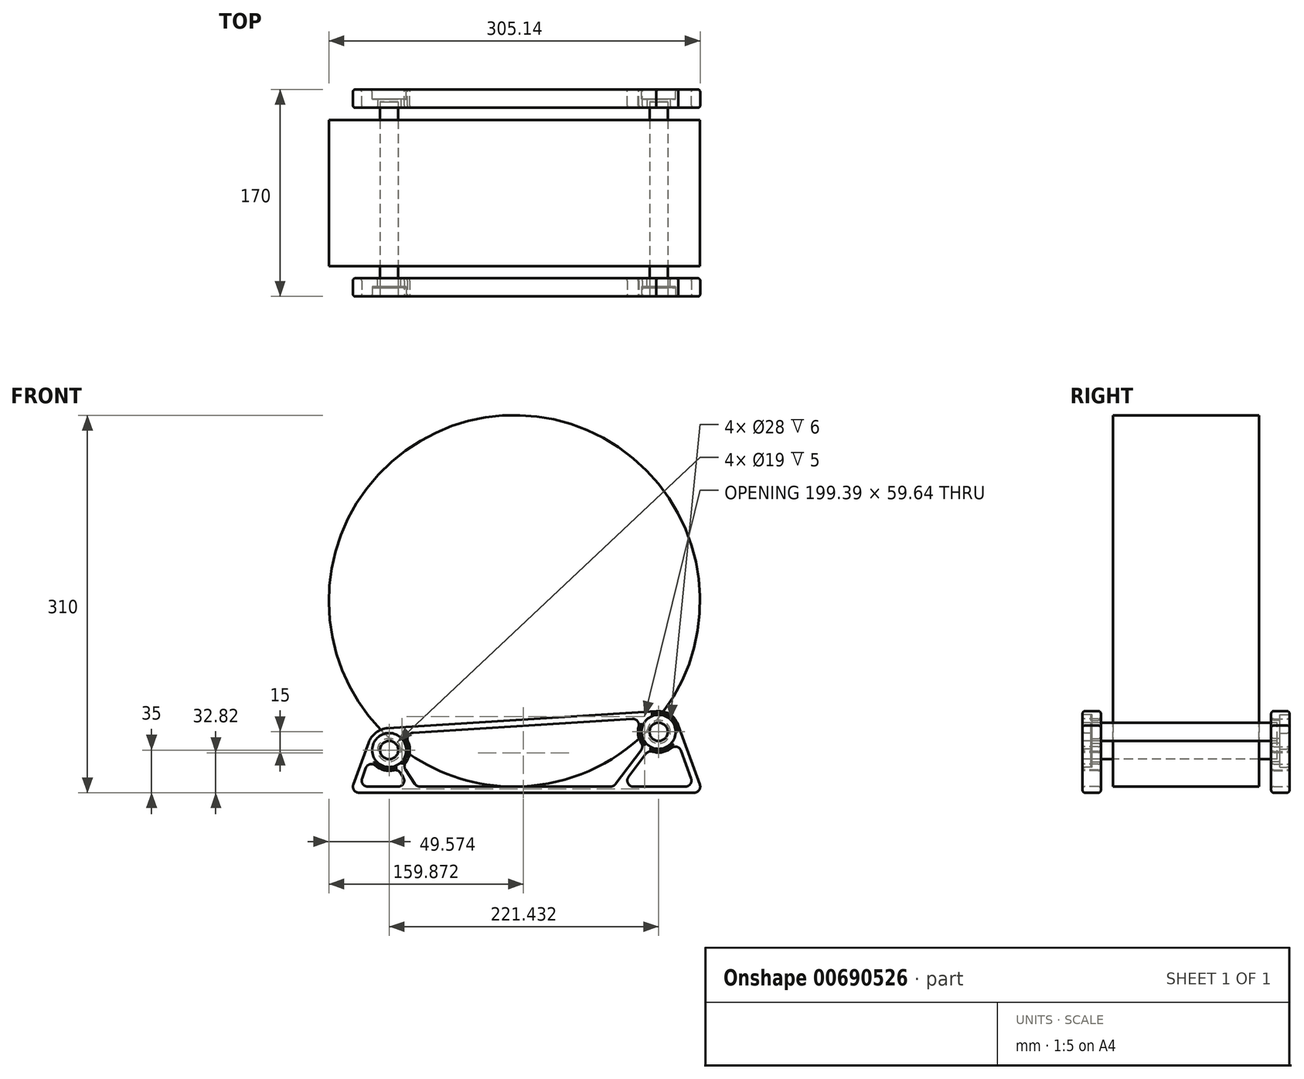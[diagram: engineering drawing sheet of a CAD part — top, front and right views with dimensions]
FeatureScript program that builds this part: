
annotation { "Feature Type Name" : "Feature", "Feature Type Description" : "" }
export const myFeature = defineFeature(function(context is Context, id is Id, definition is map)
    precondition{}
    {
        {
            var Q0;
            Q0=qCreatedBy(makeId("Front.planeOp"),FACE);
            var sketch = newSketch(context, id + "F0", { "sketchPlane" : qUnion([Q0])});
            skCircle(sketch, "E0", {"center": v(0, 0) * mm, "radius": 152.5 * mm});
            skSolve(sketch);
        }
        {
            var Q0;
            Q0=makeQuery(id+"F0.imprint","IMPRINT",FACE,{"disambiguationData":[TD([[makeQuery(id+"F0.imprint","IMPRINT",EDGE,{"derivedFrom":sQuery(id+"F0.wireOp",EDGE,"E0")}),1.0]])]});
            extrude(context, id + "F1", {"entities" : qUnion([Q0]), "endBound" : BoundingType.SYMMETRIC, "depth" : 120 * mm, "offsetDistance" : 25 * mm});
        }
        {
            var Q0;
            Q0=makeQuery(id+"F1.opExtrude","CAP_FACE",FACE,{"disambiguationData":[OSD([sQuery(id+"F0.wireOp",EDGE,"E0")])],"isStart":false});
            var sketch = newSketch(context, id + "F2", { "sketchPlane" : qUnion([Q0])});
            skCircle(sketch, "E1", {"center": v(-102.93, -122.5) * mm, "radius": 7.5 * mm});
            skCircle(sketch, "E2", {"center": v(118.5, -107.5) * mm, "radius": 7.5 * mm});
            skLineSegment(sketch, "E3", {"start": v(0, 0) * mm, "end": v(0, -152.5) * mm, "construction": true});
            skSolve(sketch);
        }
        {
            var Q0;
            Q0 = qSketchRegion(id + "F2", true);
            var Q1;
            Q1=makeQuery(id+"F1.opExtrude","CAP_FACE",FACE,{"disambiguationData":[OSD([sQuery(id+"F0.wireOp",EDGE,"E0")])],"isStart":true});
            extrude(context, id + "F3", {"entities" : qUnion([Q0]), "endBound" : BoundingType.UP_TO_SURFACE, "oppositeDirection" : true, "depth" : 15 * mm, "endBoundEntityFace" : qUnion([Q1]), "hasOffset" : true, "offsetDistance" : 15 * mm, "offsetOppositeDirection" : true, "hasSecondDirection" : true, "secondDirectionOppositeDirection" : false, "secondDirectionDepth" : 25 * mm});
        }
        {
            var Q0;
            Q0=makeQuery(id+"F3.opExtrude","CAP_FACE",FACE,{"disambiguationData":[OSD([sQuery(id+"F2.wireOp",EDGE,"E1")])],"isStart":true});
            var sketch = newSketch(context, id + "F4", { "sketchPlane" : qUnion([Q0])});
            skCircle(sketch, "E4", {"center": v(-102.93, -122.5) * mm, "radius": 7.5 * mm});
            skCircle(sketch, "E5", {"center": v(-102.93, -122.5) * mm, "radius": 14 * mm});
            skCircle(sketch, "E6", {"center": v(118.5, -107.5) * mm, "radius": 7.5 * mm});
            skCircle(sketch, "E7", {"center": v(118.5, -107.5) * mm, "radius": 14 * mm});
            skSolve(sketch);
        }
        {
            var Q0;
            Q0 = qSketchRegion(id + "F4", true);
            extrude(context, id + "F5", {"entities" : qUnion([Q0]), "oppositeDirection" : true, "depth" : 7 * mm, "offsetDistance" : 25 * mm});
        }
        {
            var Q0;
            Q0=makeQuery(id+"F5.opExtrude","CAP_FACE",FACE,{"disambiguationData":[OSD([sQuery(id+"F4.wireOp",EDGE,"E4"),sQuery(id+"F4.wireOp",EDGE,"E5")])],"isStart":true});
            var sketch = newSketch(context, id + "F6", { "sketchPlane" : qUnion([Q0])});
            skCircle(sketch, "E8", {"center": v(-102.93, -122.5) * mm, "radius": 14 * mm});
            skArc(sketch, "E9", {"start": v(-104.06, -104.54) * mm, "mid": v(-113.7, -108.09) * mm, "end": v(-119.84, -116.34) * mm});
            skCircle(sketch, "E10", {"center": v(118.5, -107.5) * mm, "radius": 14 * mm});
            skArc(sketch, "E11", {"start": v(134.73, -102.4) * mm, "mid": v(127.67, -93.5) * mm, "end": v(116.68, -90.6) * mm});
            skLineSegment(sketch, "E12", {"start": v(-127.68, -157.5) * mm, "end": v(147.64, -157.5) * mm});
            skLineSegment(sketch, "E13", {"start": v(-132.38, -150.79) * mm, "end": v(-119.84, -116.34) * mm});
            skLineSegment(sketch, "E14", {"start": v(134.73, -102.4) * mm, "end": v(152.34, -150.79) * mm});
            skLineSegment(sketch, "E15", {"start": v(-104.06, -104.54) * mm, "end": v(116.68, -90.6) * mm});
            skLineSegment(sketch, "E16", {"start": v(-93.62, -136.72) * mm, "end": v(-83.3, -152.5) * mm, "construction": true});
            skLineSegment(sketch, "E17", {"start": v(110.08, -118.68) * mm, "end": v(80.83, -157.5) * mm, "construction": true});
            skLineSegment(sketch, "E18.0", {"start": v(-120.54, -152.5) * mm, "end": v(-95.53, -152.5) * mm});
            skLineSegment(sketch, "E18.2", {"start": v(-83.3, -108.23) * mm, "end": v(96.93, -96.86) * mm});
            skLineSegment(sketch, "E18.3", {"start": v(-125.24, -145.79) * mm, "end": v(-122.15, -137.31) * mm});
            skLineSegment(sketch, "E18.5", {"start": v(136.9, -123) * mm, "end": v(145.2, -145.79) * mm});
            skArc(sketch, "E19.0", {"start": v(-114.15, -135.27) * mm, "mid": v(-107.05, -139) * mm, "end": v(-99.02, -139.05) * mm});
            skLineSegment(sketch, "E20.0", {"start": v(-93.7, -141.17) * mm, "end": v(-91.35, -144.76) * mm});
            skLineSegment(sketch, "E21.0", {"start": v(-89.5, -138.44) * mm, "end": v(-81.79, -150.24) * mm});
            skLineSegment(sketch, "E22.trimOffspring", {"start": v(-77.6, -152.5) * mm, "end": v(78.97, -152.5) * mm});
            skArc(sketch, "E23.trimOffspring", {"start": v(-89.33, -132.7) * mm, "mid": v(-86.02, -124.27) * mm, "end": v(-87.51, -115.33) * mm});
            skArc(sketch, "E24.0", {"start": v(102.08, -103.13) * mm, "mid": v(101.72, -110.18) * mm, "end": v(104.26, -116.78) * mm});
            skArc(sketch, "E25.trimOffspring", {"start": v(134.73, -102.4) * mm, "mid": v(127.81, -93.27) * mm, "end": v(116.68, -90.6) * mm});
            skLineSegment(sketch, "E26.0", {"start": v(104.06, -122.51) * mm, "end": v(82.97, -150.5) * mm});
            skLineSegment(sketch, "E27.0", {"start": v(108.06, -125.52) * mm, "end": v(93.76, -144.5) * mm});
            skArc(sketch, "E28.trimOffspring", {"start": v(113.52, -123.75) * mm, "mid": v(121.67, -124.2) * mm, "end": v(129.1, -120.8) * mm});
            skLineSegment(sketch, "E29.trimOffspring", {"start": v(97.76, -152.5) * mm, "end": v(140.5, -152.5) * mm});
            skPoint(sketch, "E30.visualSharp", {"position": v(-95.81, -137.94) * mm});
            skArc(sketch, "E30.filletArc", {"start": v(-93.7, -141.17) * mm, "mid": v(-96.02, -139.27) * mm, "end": v(-99.02, -139.05) * mm});
            skPoint(sketch, "E31.visualSharp", {"position": v(-118.89, -128.35) * mm});
            skArc(sketch, "E31.filletArc", {"start": v(-114.15, -135.27) * mm, "mid": v(-118.7, -134.18) * mm, "end": v(-122.15, -137.31) * mm});
            skPoint(sketch, "E32.visualSharp", {"position": v(-127.68, -152.5) * mm});
            skArc(sketch, "E32.filletArc", {"start": v(-125.24, -145.79) * mm, "mid": v(-124.63, -150.37) * mm, "end": v(-120.54, -152.5) * mm});
            skPoint(sketch, "E33.visualSharp", {"position": v(-86.28, -152.5) * mm});
            skArc(sketch, "E33.filletArc", {"start": v(-95.53, -152.5) * mm, "mid": v(-91.13, -149.88) * mm, "end": v(-91.35, -144.76) * mm});
            skPoint(sketch, "E34.visualSharp", {"position": v(-91.63, -135.2) * mm});
            skArc(sketch, "E34.filletArc", {"start": v(-89.33, -132.7) * mm, "mid": v(-90.32, -135.54) * mm, "end": v(-89.5, -138.44) * mm});
            skPoint(sketch, "E35.visualSharp", {"position": v(-92.81, -108.84) * mm});
            skArc(sketch, "E35.filletArc", {"start": v(-83.3, -108.23) * mm, "mid": v(-87.28, -110.67) * mm, "end": v(-87.51, -115.33) * mm});
            skPoint(sketch, "E36.visualSharp", {"position": v(-80.3, -152.5) * mm});
            skArc(sketch, "E36.filletArc", {"start": v(-81.79, -150.24) * mm, "mid": v(-79.98, -151.9) * mm, "end": v(-77.6, -152.5) * mm});
            skPoint(sketch, "E37.visualSharp", {"position": v(87.73, -152.5) * mm});
            skArc(sketch, "E37.filletArc", {"start": v(93.76, -144.5) * mm, "mid": v(93.28, -149.73) * mm, "end": v(97.76, -152.5) * mm});
            skPoint(sketch, "E38.visualSharp", {"position": v(81.47, -152.5) * mm});
            skArc(sketch, "E38.filletArc", {"start": v(78.97, -152.5) * mm, "mid": v(81.2, -151.97) * mm, "end": v(82.97, -150.5) * mm});
            skPoint(sketch, "E39.visualSharp", {"position": v(105.72, -96.3) * mm});
            skArc(sketch, "E39.filletArc", {"start": v(102.08, -103.13) * mm, "mid": v(101.11, -98.67) * mm, "end": v(96.93, -96.86) * mm});
            skPoint(sketch, "E40.visualSharp", {"position": v(110.38, -122.43) * mm});
            skArc(sketch, "E40.filletArc", {"start": v(113.52, -123.75) * mm, "mid": v(110.5, -123.77) * mm, "end": v(108.06, -125.52) * mm});
            skPoint(sketch, "E41.visualSharp", {"position": v(106.4, -119.42) * mm});
            skArc(sketch, "E41.filletArc", {"start": v(104.06, -122.51) * mm, "mid": v(105.07, -119.68) * mm, "end": v(104.26, -116.78) * mm});
            skPoint(sketch, "E42.visualSharp", {"position": v(133.9, -114.73) * mm});
            skArc(sketch, "E42.filletArc", {"start": v(136.9, -123) * mm, "mid": v(133.56, -119.9) * mm, "end": v(129.1, -120.8) * mm});
            skPoint(sketch, "E43.visualSharp", {"position": v(147.64, -152.5) * mm});
            skArc(sketch, "E43.filletArc", {"start": v(140.5, -152.5) * mm, "mid": v(144.6, -150.37) * mm, "end": v(145.2, -145.79) * mm});
            skPoint(sketch, "E44.visualSharp", {"position": v(154.78, -157.5) * mm});
            skArc(sketch, "E44.filletArc", {"start": v(147.64, -157.5) * mm, "mid": v(151.73, -155.37) * mm, "end": v(152.34, -150.79) * mm});
            skPoint(sketch, "E45.visualSharp", {"position": v(-134.82, -157.5) * mm});
            skArc(sketch, "E45.filletArc", {"start": v(-132.38, -150.79) * mm, "mid": v(-131.78, -155.37) * mm, "end": v(-127.68, -157.5) * mm});
            skSolve(sketch);
        }
        {
            var Q0;
            Q0 = qSketchRegion(id + "F6", true);
            extrude(context, id + "F7", {"entities" : qUnion([Q0]), "oppositeDirection" : true, "depth" : 15 * mm, "offsetDistance" : 25 * mm});
        }
        {
            var Q0;
            Q0=makeQuery(id+"F7.opExtrude","CAP_FACE",FACE,{"disambiguationData":[OSD([sQuery(id+"F6.wireOp",EDGE,"E8"),sQuery(id+"F6.wireOp",EDGE,"E10"),sQuery(id+"F6.wireOp",EDGE,"E12"),sQuery(id+"F6.wireOp",EDGE,"E13"),sQuery(id+"F6.wireOp",EDGE,"E14"),sQuery(id+"F6.wireOp",EDGE,"E15"),sQuery(id+"F6.wireOp",EDGE,"E18.0"),sQuery(id+"F6.wireOp",EDGE,"E18.2"),sQuery(id+"F6.wireOp",EDGE,"E18.3"),sQuery(id+"F6.wireOp",EDGE,"E18.5"),sQuery(id+"F6.wireOp",EDGE,"E19.0"),sQuery(id+"F6.wireOp",EDGE,"E9"),sQuery(id+"F6.wireOp",EDGE,"E20.0"),sQuery(id+"F6.wireOp",EDGE,"E21.0"),sQuery(id+"F6.wireOp",EDGE,"E22.trimOffspring"),sQuery(id+"F6.wireOp",EDGE,"E23.trimOffspring"),sQuery(id+"F6.wireOp",EDGE,"E24.0"),sQuery(id+"F6.wireOp",EDGE,"E25.trimOffspring"),sQuery(id+"F6.wireOp",EDGE,"E26.0"),sQuery(id+"F6.wireOp",EDGE,"E27.0"),sQuery(id+"F6.wireOp",EDGE,"E28.trimOffspring"),sQuery(id+"F6.wireOp",EDGE,"E29.trimOffspring"),sQuery(id+"F6.wireOp",EDGE,"E30.filletArc"),sQuery(id+"F6.wireOp",EDGE,"E31.filletArc"),sQuery(id+"F6.wireOp",EDGE,"E32.filletArc"),sQuery(id+"F6.wireOp",EDGE,"E33.filletArc"),sQuery(id+"F6.wireOp",EDGE,"E34.filletArc"),sQuery(id+"F6.wireOp",EDGE,"E35.filletArc"),sQuery(id+"F6.wireOp",EDGE,"E36.filletArc"),sQuery(id+"F6.wireOp",EDGE,"E37.filletArc"),sQuery(id+"F6.wireOp",EDGE,"E38.filletArc"),sQuery(id+"F6.wireOp",EDGE,"E39.filletArc"),sQuery(id+"F6.wireOp",EDGE,"E40.filletArc"),sQuery(id+"F6.wireOp",EDGE,"E41.filletArc"),sQuery(id+"F6.wireOp",EDGE,"E42.filletArc"),sQuery(id+"F6.wireOp",EDGE,"E43.filletArc"),sQuery(id+"F6.wireOp",EDGE,"E44.filletArc"),sQuery(id+"F6.wireOp",EDGE,"E45.filletArc")])],"isStart":false});
            var sketch = newSketch(context, id + "F8", { "sketchPlane" : qUnion([Q0])});
            skCircle(sketch, "E46", {"center": v(-118.5, -107.5) * mm, "radius": 9.5 * mm});
            skCircle(sketch, "E47", {"center": v(102.93, -122.5) * mm, "radius": 9.5 * mm});
            skSolve(sketch);
        }
        {
            var Q0;
            Q0=makeQuery(id+"F8.imprint","IMPRINT",FACE,{"disambiguationData":[TD([[makeQuery(id+"F8.imprint","IMPRINT",EDGE,{"derivedFrom":sQuery(id+"F8.wireOp",EDGE,"E46")}),-1.0]])]});
            var Q1;
            Q1=makeQuery(id+"F8.imprint","IMPRINT",FACE,{"disambiguationData":[TD([[makeQuery(id+"F8.imprint","IMPRINT",EDGE,{"derivedFrom":sQuery(id+"F8.wireOp",EDGE,"E47")}),-1.0]])]});
            var Q2;
            Q2=makeQuery(id+"F5.opExtrude","CAP_FACE",FACE,{"disambiguationData":[OSD([sQuery(id+"F4.wireOp",EDGE,"E6"),sQuery(id+"F4.wireOp",EDGE,"E7")])],"isStart":false});
            extrude(context, id + "F9", {"entities" : qUnion([Q0, Q1]), "operationType" : NewBodyOperationType.ADD, "endBound" : BoundingType.UP_TO_SURFACE, "oppositeDirection" : true, "depth" : 25 * mm, "endBoundEntityFace" : qUnion([Q2]), "hasOffset" : true, "offsetDistance" : 1 * mm});
        }
        {
            var Q0;
            {var subQ0=sQuery(id+"F6.wireOp",EDGE,"E8");var subQ1=sQuery(id+"F6.wireOp",EDGE,"E10");Q0=makeQuery(id+"F9.boolean.opBoolean","MERGE",FACE,{"derivedFrom":[makeQuery(id+"F7.opExtrude","CAP_FACE",FACE,{"disambiguationData":[OSD([subQ0,subQ1,sQuery(id+"F6.wireOp",EDGE,"E12"),sQuery(id+"F6.wireOp",EDGE,"E13"),sQuery(id+"F6.wireOp",EDGE,"E14"),sQuery(id+"F6.wireOp",EDGE,"E15"),sQuery(id+"F6.wireOp",EDGE,"E18.0"),sQuery(id+"F6.wireOp",EDGE,"E18.2"),sQuery(id+"F6.wireOp",EDGE,"E18.3"),sQuery(id+"F6.wireOp",EDGE,"E18.5"),sQuery(id+"F6.wireOp",EDGE,"E19.0"),sQuery(id+"F6.wireOp",EDGE,"E9"),sQuery(id+"F6.wireOp",EDGE,"E20.0"),sQuery(id+"F6.wireOp",EDGE,"E21.0"),sQuery(id+"F6.wireOp",EDGE,"E22.trimOffspring"),sQuery(id+"F6.wireOp",EDGE,"E23.trimOffspring"),sQuery(id+"F6.wireOp",EDGE,"E24.0"),sQuery(id+"F6.wireOp",EDGE,"E25.trimOffspring"),sQuery(id+"F6.wireOp",EDGE,"E26.0"),sQuery(id+"F6.wireOp",EDGE,"E27.0"),sQuery(id+"F6.wireOp",EDGE,"E28.trimOffspring"),sQuery(id+"F6.wireOp",EDGE,"E29.trimOffspring"),sQuery(id+"F6.wireOp",EDGE,"E30.filletArc"),sQuery(id+"F6.wireOp",EDGE,"E31.filletArc"),sQuery(id+"F6.wireOp",EDGE,"E32.filletArc"),sQuery(id+"F6.wireOp",EDGE,"E33.filletArc"),sQuery(id+"F6.wireOp",EDGE,"E34.filletArc"),sQuery(id+"F6.wireOp",EDGE,"E35.filletArc"),sQuery(id+"F6.wireOp",EDGE,"E36.filletArc"),sQuery(id+"F6.wireOp",EDGE,"E37.filletArc"),sQuery(id+"F6.wireOp",EDGE,"E38.filletArc"),sQuery(id+"F6.wireOp",EDGE,"E39.filletArc"),sQuery(id+"F6.wireOp",EDGE,"E40.filletArc"),sQuery(id+"F6.wireOp",EDGE,"E41.filletArc"),sQuery(id+"F6.wireOp",EDGE,"E42.filletArc"),sQuery(id+"F6.wireOp",EDGE,"E43.filletArc"),sQuery(id+"F6.wireOp",EDGE,"E44.filletArc"),sQuery(id+"F6.wireOp",EDGE,"E45.filletArc")])],"isStart":false}),makeQuery(id+"F9.opExtrude","CAP_FACE",FACE,{"disambiguationData":[OSD([subQ1,sQuery(id+"F8.wireOp",EDGE,"E46")])],"isStart":true}),makeQuery(id+"F9.opExtrude","CAP_FACE",FACE,{"disambiguationData":[OSD([subQ0,sQuery(id+"F8.wireOp",EDGE,"E47")])],"isStart":true})]});}
            fillet(context, id + "F10", {"entities" : qUnion([Q0]), "radius" : 2 * mm, "tangentPropagation" : true, "allowEdgeOverflow" : false});
        }
        {
            var Q0;
            Q0=makeQuery(id+"F7.opExtrude","CAP_FACE",FACE,{"disambiguationData":[OSD([sQuery(id+"F6.wireOp",EDGE,"E8"),sQuery(id+"F6.wireOp",EDGE,"E10"),sQuery(id+"F6.wireOp",EDGE,"E12"),sQuery(id+"F6.wireOp",EDGE,"E13"),sQuery(id+"F6.wireOp",EDGE,"E14"),sQuery(id+"F6.wireOp",EDGE,"E15"),sQuery(id+"F6.wireOp",EDGE,"E18.0"),sQuery(id+"F6.wireOp",EDGE,"E18.2"),sQuery(id+"F6.wireOp",EDGE,"E18.3"),sQuery(id+"F6.wireOp",EDGE,"E18.5"),sQuery(id+"F6.wireOp",EDGE,"E19.0"),sQuery(id+"F6.wireOp",EDGE,"E9"),sQuery(id+"F6.wireOp",EDGE,"E20.0"),sQuery(id+"F6.wireOp",EDGE,"E21.0"),sQuery(id+"F6.wireOp",EDGE,"E22.trimOffspring"),sQuery(id+"F6.wireOp",EDGE,"E23.trimOffspring"),sQuery(id+"F6.wireOp",EDGE,"E24.0"),sQuery(id+"F6.wireOp",EDGE,"E25.trimOffspring"),sQuery(id+"F6.wireOp",EDGE,"E26.0"),sQuery(id+"F6.wireOp",EDGE,"E27.0"),sQuery(id+"F6.wireOp",EDGE,"E28.trimOffspring"),sQuery(id+"F6.wireOp",EDGE,"E29.trimOffspring"),sQuery(id+"F6.wireOp",EDGE,"E30.filletArc"),sQuery(id+"F6.wireOp",EDGE,"E31.filletArc"),sQuery(id+"F6.wireOp",EDGE,"E32.filletArc"),sQuery(id+"F6.wireOp",EDGE,"E33.filletArc"),sQuery(id+"F6.wireOp",EDGE,"E34.filletArc"),sQuery(id+"F6.wireOp",EDGE,"E35.filletArc"),sQuery(id+"F6.wireOp",EDGE,"E36.filletArc"),sQuery(id+"F6.wireOp",EDGE,"E37.filletArc"),sQuery(id+"F6.wireOp",EDGE,"E38.filletArc"),sQuery(id+"F6.wireOp",EDGE,"E39.filletArc"),sQuery(id+"F6.wireOp",EDGE,"E40.filletArc"),sQuery(id+"F6.wireOp",EDGE,"E41.filletArc"),sQuery(id+"F6.wireOp",EDGE,"E42.filletArc"),sQuery(id+"F6.wireOp",EDGE,"E43.filletArc"),sQuery(id+"F6.wireOp",EDGE,"E44.filletArc"),sQuery(id+"F6.wireOp",EDGE,"E45.filletArc")])],"isStart":true});
            fillet(context, id + "F11", {"entities" : qUnion([Q0]), "radius" : 2 * mm, "tangentPropagation" : true, "allowEdgeOverflow" : false});
        }
        {
            var Q0;
            Q0=makeQuery(id+"F7.opExtrude","SWEPT_BODY",BODY,{"disambiguationData":[OSD([sQuery(id+"F6.wireOp",EDGE,"E8"),sQuery(id+"F6.wireOp",EDGE,"E10"),sQuery(id+"F6.wireOp",EDGE,"E12"),sQuery(id+"F6.wireOp",EDGE,"E13"),sQuery(id+"F6.wireOp",EDGE,"E14"),sQuery(id+"F6.wireOp",EDGE,"E15"),sQuery(id+"F6.wireOp",EDGE,"E18.0"),sQuery(id+"F6.wireOp",EDGE,"E18.2"),sQuery(id+"F6.wireOp",EDGE,"E18.3"),sQuery(id+"F6.wireOp",EDGE,"E18.5"),sQuery(id+"F6.wireOp",EDGE,"E19.0"),sQuery(id+"F6.wireOp",EDGE,"E9"),sQuery(id+"F6.wireOp",EDGE,"E20.0"),sQuery(id+"F6.wireOp",EDGE,"E21.0"),sQuery(id+"F6.wireOp",EDGE,"E22.trimOffspring"),sQuery(id+"F6.wireOp",EDGE,"E23.trimOffspring"),sQuery(id+"F6.wireOp",EDGE,"E24.0"),sQuery(id+"F6.wireOp",EDGE,"E25.trimOffspring"),sQuery(id+"F6.wireOp",EDGE,"E26.0"),sQuery(id+"F6.wireOp",EDGE,"E27.0"),sQuery(id+"F6.wireOp",EDGE,"E28.trimOffspring"),sQuery(id+"F6.wireOp",EDGE,"E29.trimOffspring"),sQuery(id+"F6.wireOp",EDGE,"E30.filletArc"),sQuery(id+"F6.wireOp",EDGE,"E31.filletArc"),sQuery(id+"F6.wireOp",EDGE,"E32.filletArc"),sQuery(id+"F6.wireOp",EDGE,"E33.filletArc"),sQuery(id+"F6.wireOp",EDGE,"E34.filletArc"),sQuery(id+"F6.wireOp",EDGE,"E35.filletArc"),sQuery(id+"F6.wireOp",EDGE,"E36.filletArc"),sQuery(id+"F6.wireOp",EDGE,"E37.filletArc"),sQuery(id+"F6.wireOp",EDGE,"E38.filletArc"),sQuery(id+"F6.wireOp",EDGE,"E39.filletArc"),sQuery(id+"F6.wireOp",EDGE,"E40.filletArc"),sQuery(id+"F6.wireOp",EDGE,"E41.filletArc"),sQuery(id+"F6.wireOp",EDGE,"E42.filletArc"),sQuery(id+"F6.wireOp",EDGE,"E43.filletArc"),sQuery(id+"F6.wireOp",EDGE,"E44.filletArc"),sQuery(id+"F6.wireOp",EDGE,"E45.filletArc")])]});
            var Q1;
            Q1=qCreatedBy(makeId("Front.planeOp"),FACE);
            mirror(context, id + "F12", {"entities" : qUnion([Q0]), "mirrorPlane" : qUnion([Q1])});
        }
    });
